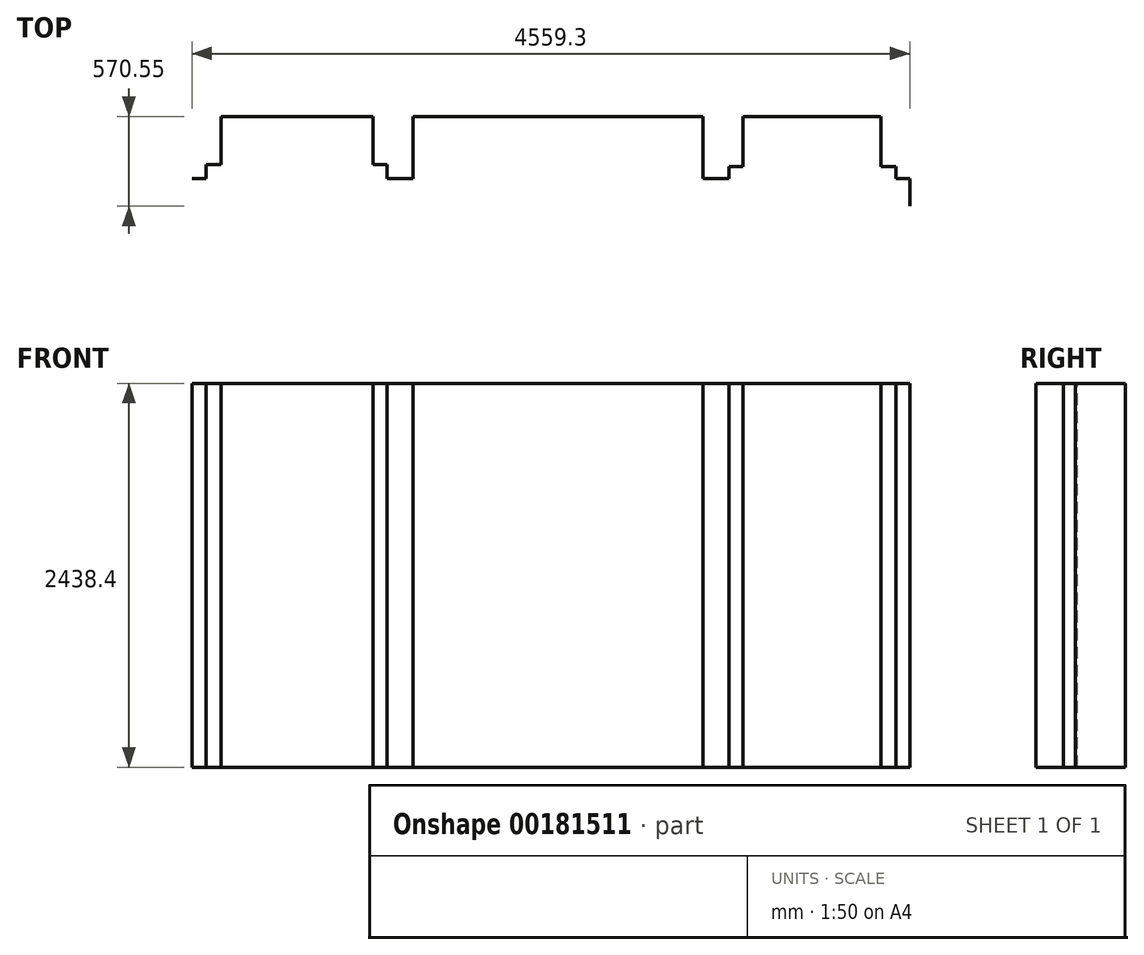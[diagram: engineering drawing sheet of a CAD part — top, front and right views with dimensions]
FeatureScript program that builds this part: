
annotation { "Feature Type Name" : "Feature", "Feature Type Description" : "" }
export const myFeature = defineFeature(function(context is Context, id is Id, definition is map)
    precondition{}
    {
        {
            var Q0;
            Q0=qCreatedBy(makeId("Top.planeOp"),FACE);
            var sketch = newSketch(context, id + "F0", { "sketchPlane" : qUnion([Q0])});
            skLineSegment(sketch, "E0", {"start": v(0, 0) * mm, "end": v(88.9, 0) * mm});
            skLineSegment(sketch, "E1", {"start": v(88.9, 0) * mm, "end": v(88.9, 88.9) * mm});
            skLineSegment(sketch, "E2", {"start": v(88.9, 88.9) * mm, "end": v(184.15, 88.9) * mm});
            skLineSegment(sketch, "E3", {"start": v(184.15, 88.9) * mm, "end": v(184.15, 393.7) * mm});
            skLineSegment(sketch, "E4", {"start": v(184.15, 393.7) * mm, "end": v(1149.35, 393.7) * mm});
            skLineSegment(sketch, "E5", {"start": v(1149.35, 393.7) * mm, "end": v(1149.35, 88.9) * mm});
            skLineSegment(sketch, "E6", {"start": v(1149.35, 88.9) * mm, "end": v(1238.25, 88.9) * mm});
            skLineSegment(sketch, "E7", {"start": v(1238.25, 88.9) * mm, "end": v(1238.25, 0) * mm});
            skLineSegment(sketch, "E8", {"start": v(1238.25, 0) * mm, "end": v(1403.35, 0) * mm});
            skLineSegment(sketch, "E9", {"start": v(1403.35, 0) * mm, "end": v(1403.35, 393.7) * mm});
            skLineSegment(sketch, "E10", {"start": v(1403.35, 393.7) * mm, "end": v(3244.85, 393.7) * mm});
            skLineSegment(sketch, "E11", {"start": v(3244.85, 393.7) * mm, "end": v(3244.85, 0) * mm});
            skLineSegment(sketch, "E12", {"start": v(3244.85, 0) * mm, "end": v(3409.95, 0) * mm});
            skLineSegment(sketch, "E13", {"start": v(3409.95, 0) * mm, "end": v(3409.95, 76.2) * mm});
            skLineSegment(sketch, "E14", {"start": v(3409.95, 76.2) * mm, "end": v(3498.85, 76.2) * mm});
            skLineSegment(sketch, "E15", {"start": v(3498.85, 76.2) * mm, "end": v(3498.85, 393.7) * mm});
            skLineSegment(sketch, "E16", {"start": v(3498.85, 393.7) * mm, "end": v(4375.15, 393.7) * mm});
            skLineSegment(sketch, "E17", {"start": v(4375.15, 393.7) * mm, "end": v(4375.15, 76.2) * mm});
            skLineSegment(sketch, "E18", {"start": v(4375.15, 76.2) * mm, "end": v(4470.4, 76.2) * mm});
            skLineSegment(sketch, "E19", {"start": v(4470.4, 76.2) * mm, "end": v(4470.4, 0) * mm});
            skLineSegment(sketch, "E20", {"start": v(4470.4, 0) * mm, "end": v(4559.3, 0) * mm});
            skLineSegment(sketch, "E21", {"start": v(4559.3, 0) * mm, "end": v(4559.3, -176.85) * mm});
            skSolve(sketch);
        }
        {
            var Q0;
            Q0=sQuery(id+"F0.wireOp",EDGE,"E9");
            var Q1;
            Q1=sQuery(id+"F0.wireOp",EDGE,"E10");
            var Q2;
            Q2=sQuery(id+"F0.wireOp",EDGE,"E12");
            var Q3;
            Q3=sQuery(id+"F0.wireOp",EDGE,"E11");
            var Q4;
            Q4=sQuery(id+"F0.wireOp",EDGE,"E8");
            var Q5;
            Q5=sQuery(id+"F0.wireOp",EDGE,"E7");
            var Q6;
            Q6=sQuery(id+"F0.wireOp",EDGE,"E18");
            var Q7;
            Q7=sQuery(id+"F0.wireOp",EDGE,"E5");
            var Q8;
            Q8=sQuery(id+"F0.wireOp",EDGE,"E21");
            var Q9;
            Q9=sQuery(id+"F0.wireOp",EDGE,"E16");
            var Q10;
            Q10=sQuery(id+"F0.wireOp",EDGE,"E15");
            var Q11;
            Q11=sQuery(id+"F0.wireOp",EDGE,"E4");
            var Q12;
            Q12=sQuery(id+"F0.wireOp",EDGE,"E1");
            var Q13;
            Q13=sQuery(id+"F0.wireOp",EDGE,"E3");
            var Q14;
            Q14=sQuery(id+"F0.wireOp",EDGE,"E17");
            var Q15;
            Q15=sQuery(id+"F0.wireOp",EDGE,"E2");
            var Q16;
            Q16=sQuery(id+"F0.wireOp",EDGE,"E0");
            var Q17;
            Q17=sQuery(id+"F0.wireOp",EDGE,"E6");
            var Q18;
            Q18=sQuery(id+"F0.wireOp",EDGE,"E14");
            var Q19;
            Q19=sQuery(id+"F0.wireOp",EDGE,"E20");
            var Q20;
            Q20=sQuery(id+"F0.wireOp",EDGE,"E13");
            var Q21;
            Q21=sQuery(id+"F0.wireOp",EDGE,"E19");
            extrude(context, id + "F1", {"bodyType" : ToolBodyType.SURFACE, "surfaceEntities" : qUnion([Q0, Q1, Q2, Q3, Q4, Q5, Q6, Q7, Q8, Q9, Q10, Q11, Q12, Q13, Q14, Q15, Q16, Q17, Q18, Q19, Q20, Q21]), "depth" : 2438.4 * mm});
        }
    });
